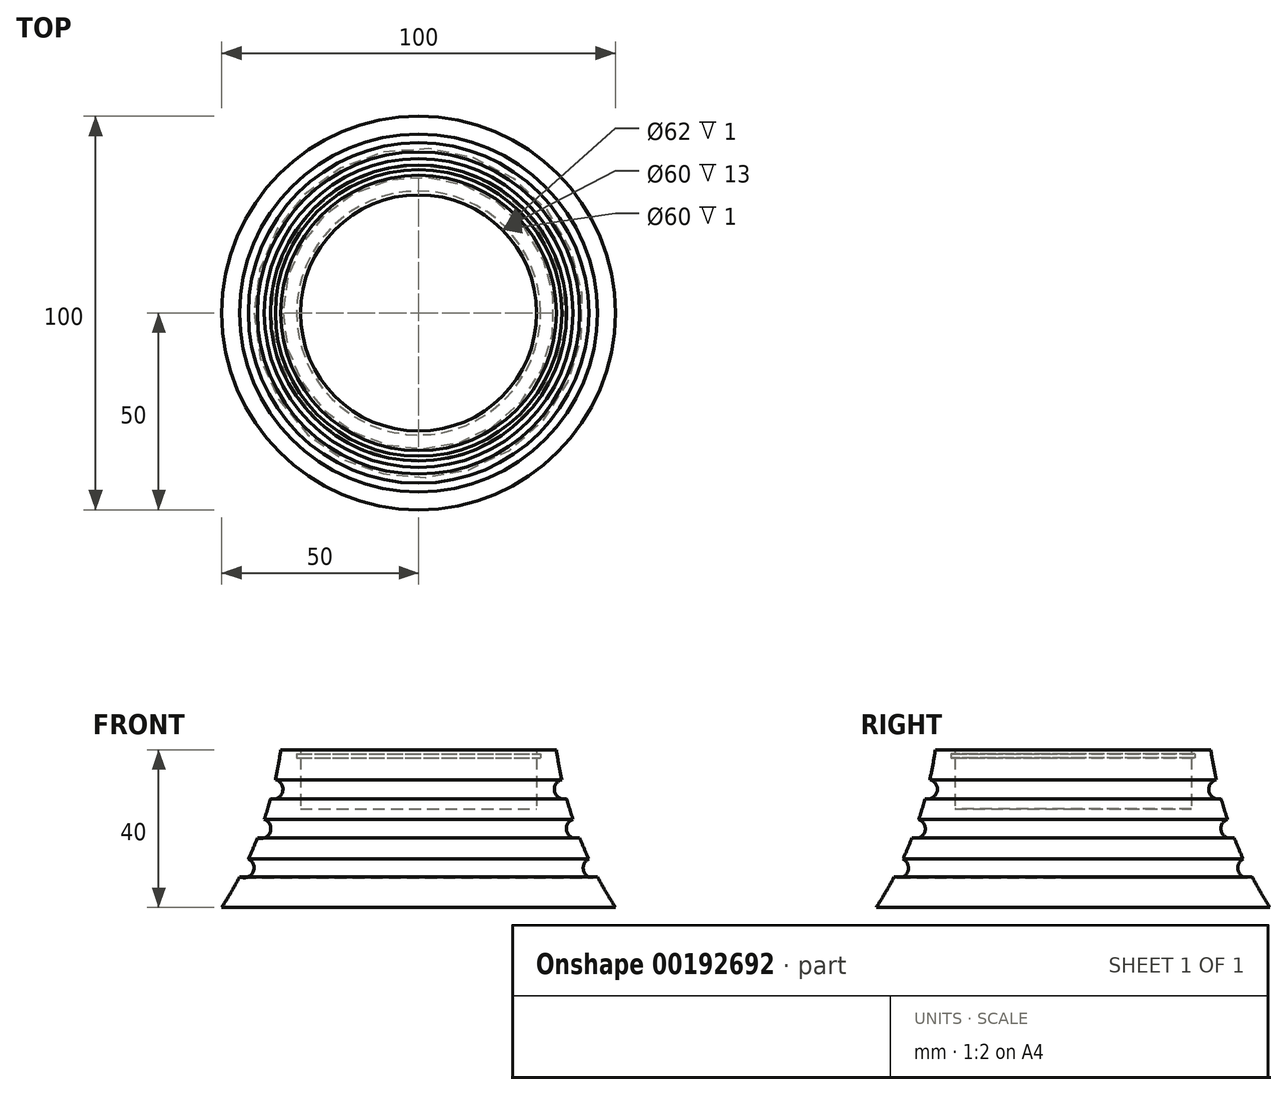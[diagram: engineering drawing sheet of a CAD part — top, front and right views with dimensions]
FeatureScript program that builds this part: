
annotation { "Feature Type Name" : "Feature", "Feature Type Description" : "" }
export const myFeature = defineFeature(function(context is Context, id is Id, definition is map)
    precondition{}
    {
        {
            var Q0;
            Q0=qCreatedBy(makeId("Front.planeOp"),FACE);
            var sketch = newSketch(context, id + "F0", { "sketchPlane" : qUnion([Q0])});
            skLineSegment(sketch, "E0", {"start": v(0, 0) * mm, "end": v(0, 25) * mm});
            skLineSegment(sketch, "E1", {"start": v(0, 25) * mm, "end": v(30, 25) * mm});
            skLineSegment(sketch, "E2", {"start": v(30, 25) * mm, "end": v(30, 38) * mm});
            skLineSegment(sketch, "E3", {"start": v(0, 0) * mm, "end": v(50, 0) * mm});
            skLineSegment(sketch, "E4", {"start": v(30, 40) * mm, "end": v(35, 40) * mm});
            skArc(sketch, "E5", {"start": v(35, 40) * mm, "mid": v(35.62, 36.2) * mm, "end": v(36.4, 32.43) * mm});
            skLineSegment(sketch, "E6.bottom", {"start": v(30, 39) * mm, "end": v(31, 39) * mm});
            skLineSegment(sketch, "E6.top", {"start": v(30, 38) * mm, "end": v(31, 38) * mm});
            skLineSegment(sketch, "E6.right", {"start": v(31, 39) * mm, "end": v(31, 38) * mm});
            skLineSegment(sketch, "E7.trimOffspring", {"start": v(30, 39) * mm, "end": v(30, 40) * mm});
            skArc(sketch, "E8", {"start": v(36.4, 32.43) * mm, "mid": v(34.54, 29.4) * mm, "end": v(37.6, 27.58) * mm});
            skArc(sketch, "E9", {"start": v(39.21, 22.36) * mm, "mid": v(37.7, 19.14) * mm, "end": v(40.93, 17.66) * mm});
            skArc(sketch, "E10", {"start": v(43.24, 12.25) * mm, "mid": v(42.08, 8.9) * mm, "end": v(45.46, 7.77) * mm});
            skArc(sketch, "E11.trimOffspring", {"start": v(40.93, 17.66) * mm, "mid": v(42.04, 14.94) * mm, "end": v(43.24, 12.25) * mm});
            skArc(sketch, "E12.trimOffspring", {"start": v(37.6, 27.58) * mm, "mid": v(38.37, 24.96) * mm, "end": v(39.21, 22.36) * mm});
            skArc(sketch, "E13.trimOffspring", {"start": v(45.46, 7.77) * mm, "mid": v(47.64, 3.84) * mm, "end": v(50, 0) * mm});
            skSolve(sketch);
        }
        {
            var Q0;
            Q0=makeQuery(id+"F0.imprint","IMPRINT",FACE,{"disambiguationData":[TD([[makeQuery(id+"F0.imprint","IMPRINT",EDGE,{"derivedFrom":sQuery(id+"F0.wireOp",EDGE,"E0")}),-1.0]])]});
            var Q1;
            Q1=sQuery(id+"F0.wireOp",EDGE,"E0");
            revolve(context, id + "F1", {"entities" : qUnion([Q0]), "axis" : qUnion([Q1]), "revolveType" : RevolveType.FULL});
        }
    });
